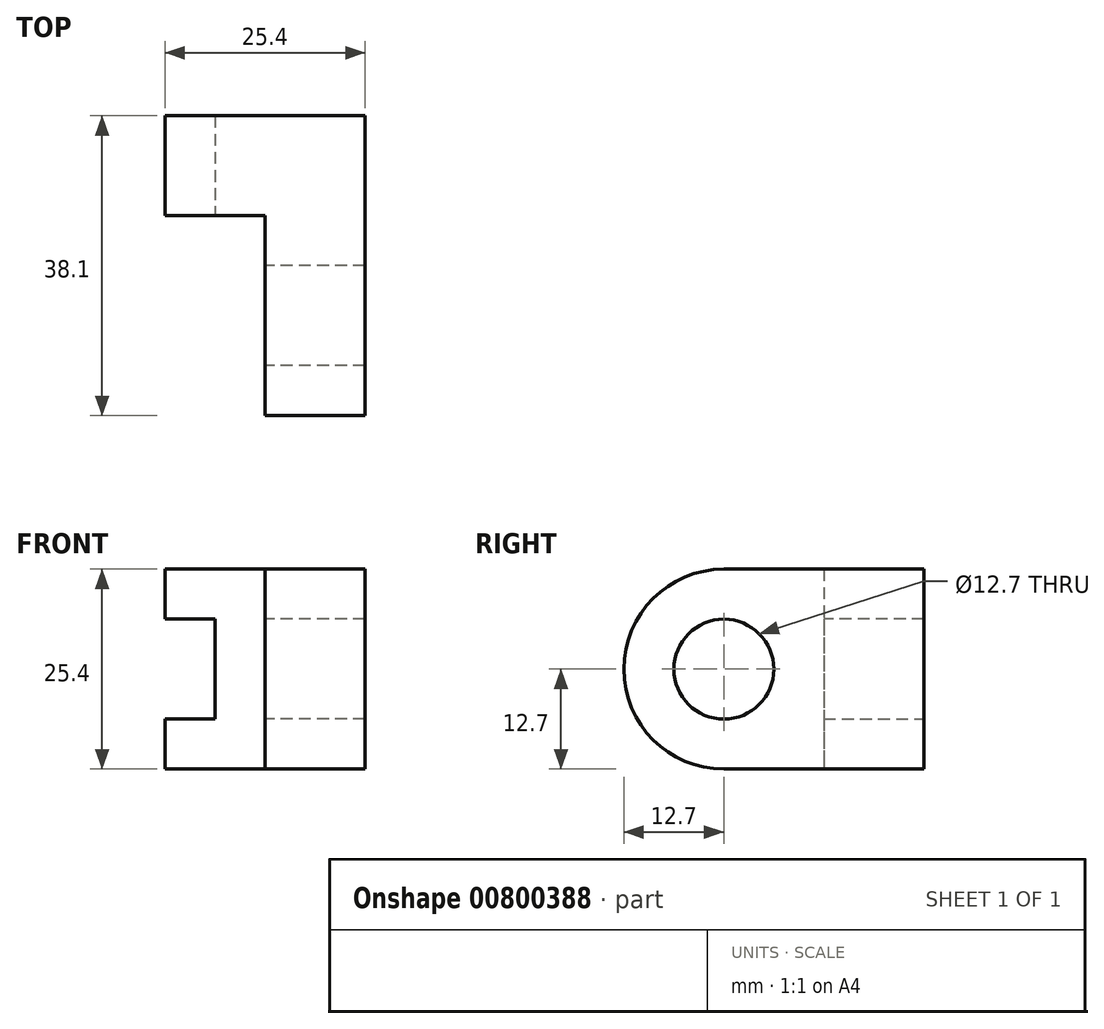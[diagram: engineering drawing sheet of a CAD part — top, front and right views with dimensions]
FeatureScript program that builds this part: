
annotation { "Feature Type Name" : "Feature", "Feature Type Description" : "" }
export const myFeature = defineFeature(function(context is Context, id is Id, definition is map)
    precondition{}
    {
        {
            var Q0;
            Q0=qCreatedBy(makeId("Top.planeOp"),FACE);
            var sketch = newSketch(context, id + "F0", { "sketchPlane" : qUnion([Q0])});
            skLineSegment(sketch, "E0", {"start": v(0, 0) * mm, "end": v(0, -12.7) * mm});
            skLineSegment(sketch, "E1", {"start": v(0, -12.7) * mm, "end": v(12.7, -12.7) * mm});
            skLineSegment(sketch, "E2", {"start": v(12.7, -12.7) * mm, "end": v(12.7, -66.38) * mm});
            skLineSegment(sketch, "E3", {"start": v(12.7, -66.38) * mm, "end": v(25.4, -66.38) * mm});
            skLineSegment(sketch, "E4", {"start": v(25.4, -66.38) * mm, "end": v(25.4, 0) * mm});
            skLineSegment(sketch, "E5", {"start": v(25.4, 0) * mm, "end": v(0, 0) * mm});
            skSolve(sketch);
        }
        {
            var Q0;
            Q0 = qSketchRegion(id + "F0", true);
            extrude(context, id + "F1", {"entities" : qUnion([Q0]), "depth" : 25.4 * mm, "offsetDistance" : 25.4 * mm});
        }
        {
            var Q0;
            Q0=makeQuery(id+"F1.opExtrude","SWEPT_FACE",FACE,{"disambiguationData":[OSD([sQuery(id+"F0.wireOp",EDGE,"E0")])]});
            var sketch = newSketch(context, id + "F2", { "sketchPlane" : qUnion([Q0])});
            skLineSegment(sketch, "E6", {"start": v(0, 12.7) * mm, "end": v(0, 6.35) * mm});
            skLineSegment(sketch, "E7", {"start": v(0, 12.7) * mm, "end": v(0, 19.05) * mm});
            skLineSegment(sketch, "E8", {"start": v(0, 19.05) * mm, "end": v(12.7, 19.05) * mm});
            skLineSegment(sketch, "E9", {"start": v(12.7, 19.05) * mm, "end": v(12.7, 6.35) * mm});
            skLineSegment(sketch, "E10", {"start": v(12.7, 6.35) * mm, "end": v(0, 6.35) * mm});
            skSolve(sketch);
        }
        {
            var Q0;
            Q0 = qSketchRegion(id + "F2", true);
            extrude(context, id + "F3", {"entities" : qUnion([Q0]), "operationType" : NewBodyOperationType.REMOVE, "oppositeDirection" : true, "depth" : 6.35 * mm, "offsetDistance" : 25.4 * mm});
        }
        {
            var Q0;
            Q0=makeQuery(id+"F1.opExtrude","SWEPT_FACE",FACE,{"disambiguationData":[OSD([sQuery(id+"F0.wireOp",EDGE,"E2")])]});
            var sketch = newSketch(context, id + "F4", { "sketchPlane" : qUnion([Q0])});
            skLineSegment(sketch, "E11", {"start": v(12.7, 25.4) * mm, "end": v(25.4, 25.4) * mm, "construction": true});
            skLineSegment(sketch, "E12", {"start": v(12.7, 0) * mm, "end": v(25.4, 0) * mm, "construction": true});
            skLineSegment(sketch, "E13", {"start": v(25.4, 25.4) * mm, "end": v(25.4, 0) * mm, "construction": true});
            skLineSegment(sketch, "E14", {"start": v(12.7, 12.7) * mm, "end": v(38.1, 12.7) * mm, "construction": true});
            skArc(sketch, "E15", {"start": v(25.4, 0) * mm, "mid": v(38.1, 12.7) * mm, "end": v(25.4, 25.4) * mm});
            skCircle(sketch, "E16", {"center": v(25.4, 12.7) * mm, "radius": 6.35 * mm});
            skSolve(sketch);
        }
        {
            var Q0;
            Q0 = qSketchRegion(id + "F4", true);
            var Q1;
            {var subQ0=sQuery(id+"F4.wireOp",EDGE,"E15");Q1=makeQuery(id+"F4.imprint","IMPRINT",FACE,{"disambiguationData":[TD([[makeQuery(id+"F4.imprint","IMPRINT",EDGE,{"derivedFrom":subQ0}),-1.0]])]});}
            extrude(context, id + "F5", {"entities" : qUnion([Q0, Q1]), "operationType" : NewBodyOperationType.REMOVE, "endBound" : BoundingType.THROUGH_ALL, "oppositeDirection" : true, "depth" : 25.4 * mm, "offsetDistance" : 25.4 * mm});
        }
    });
